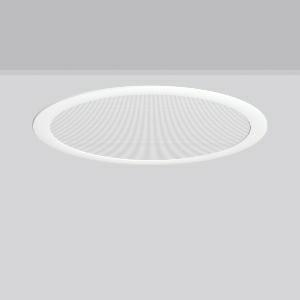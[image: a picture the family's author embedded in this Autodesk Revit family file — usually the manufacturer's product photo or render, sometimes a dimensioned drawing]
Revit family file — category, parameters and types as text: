
# Revit family: toledo_flat_round_e_901586_002_1_0fdf
name_source: partatom
category: Lighting Fixtures
units: mm (PartAtom-declared; Revit-internal decimal feet)

## family parameters
Cut with Voids When Loaded = No
Host = Face
Light Source = No
Part Type = Normal
Room Calculation Point = No
Round Connector Dimension = Use Diameter
Shared = No

## types (1)
- TOLEDO FLAT round E (1 x LED Modul 840, 3550 lm, 4000)
    Apparent Load = 30 VA
    CIE Flux Codes = 60 86 96 100 100
    Color Rendering = 80
    Color Temperature = 4000
    Default Elevation = 1800 mm
    Description = Series: TOLEDO FLAT round
Ultra thin recessed downlight. Housing: die-cast aluminium. Lightguide and diffuser made of non-yellowing PMMA, prismatic. Ceiling installation with spring system. Mounting depth depends on ceiling strength. Including separate LED converter with connecting cable 250 mm. Suitable for through-wiring with separately available accessories. Surface mounted housing as accessory for all sizes. Retrofittable decorative cylinders made of chintz fabric as accessory, optional with satin finish plastic diffuser. Through-wiring box (5 pole) available as accessory. 
Colour: white
Diameter: 495 mm
Height: 6 mm
Cut-out diameter: 470 mm
Recess height: 40-59 mm
Luminaire: recess height: 31-51 mm
Lamp: LED
Socket: without socket
Colour temperature: 4000K
Colour rendering index (CRI): 80
System power: 30 W
Rated luminous flux: 3550 lm
Luminous efficiency: 118 lm/W
Control gear: Regulated power supply
Protection class: II
Type of protection: IP 54
    Height = 0 mm  [stored 0 ft]
    Lamp = 1 x LED Modul 840
    Lamp Light Flux = 3550 lm
    Lamp count = 1
    Length = 495 mm
    Lifetime = 50000 h
    Luminous efficacy = 118 lm/W
    Manufacturer = RZB
    ModVariant = No
    Model = 901586.002.1
    Mounting Place = Ceiling
    Mounting Type = Recessed
    Number of Poles = 1
    OnlyDefault = Yes
    Power Factor = 1
    Product Name = TOLEDO FLAT round E
    Product group = Recessed downlights
    ProductGroupID = 402
    Protection Class = Protection class II
    Protection Degree = IP 20
    RLX_Detail_Level = 1
    RLX_Emergency_Light_Flux = 0 lm
    RLX_Emergency_Type = 0
    RLX_Emergency_Type_DB = No
    RlxData = <blob elided: 38457 chars, md5=5191860a>
    Socket = socket
    Standby Power = 0 W
    System Light Flux = 3550 lm
    System Power = 30 W
    Type Comments = Product without accessories
    Type Image = 901586.002.jpg
    URL = http://relux.com
    VarID = ---
    Voltage = 230 V
    Voltage Range = 220-240 V
    Weight = 0.00 kg
    Width = 0 mm  [stored 0 ft]

note: [stored X ft] marks values corroborated as IEEE doubles in the binary element streams (Revit-internal decimal feet)

## geometry (parser evidence)
native form markers: Blend x4, Sweep x9
no freeform markers — native parametric forms only
